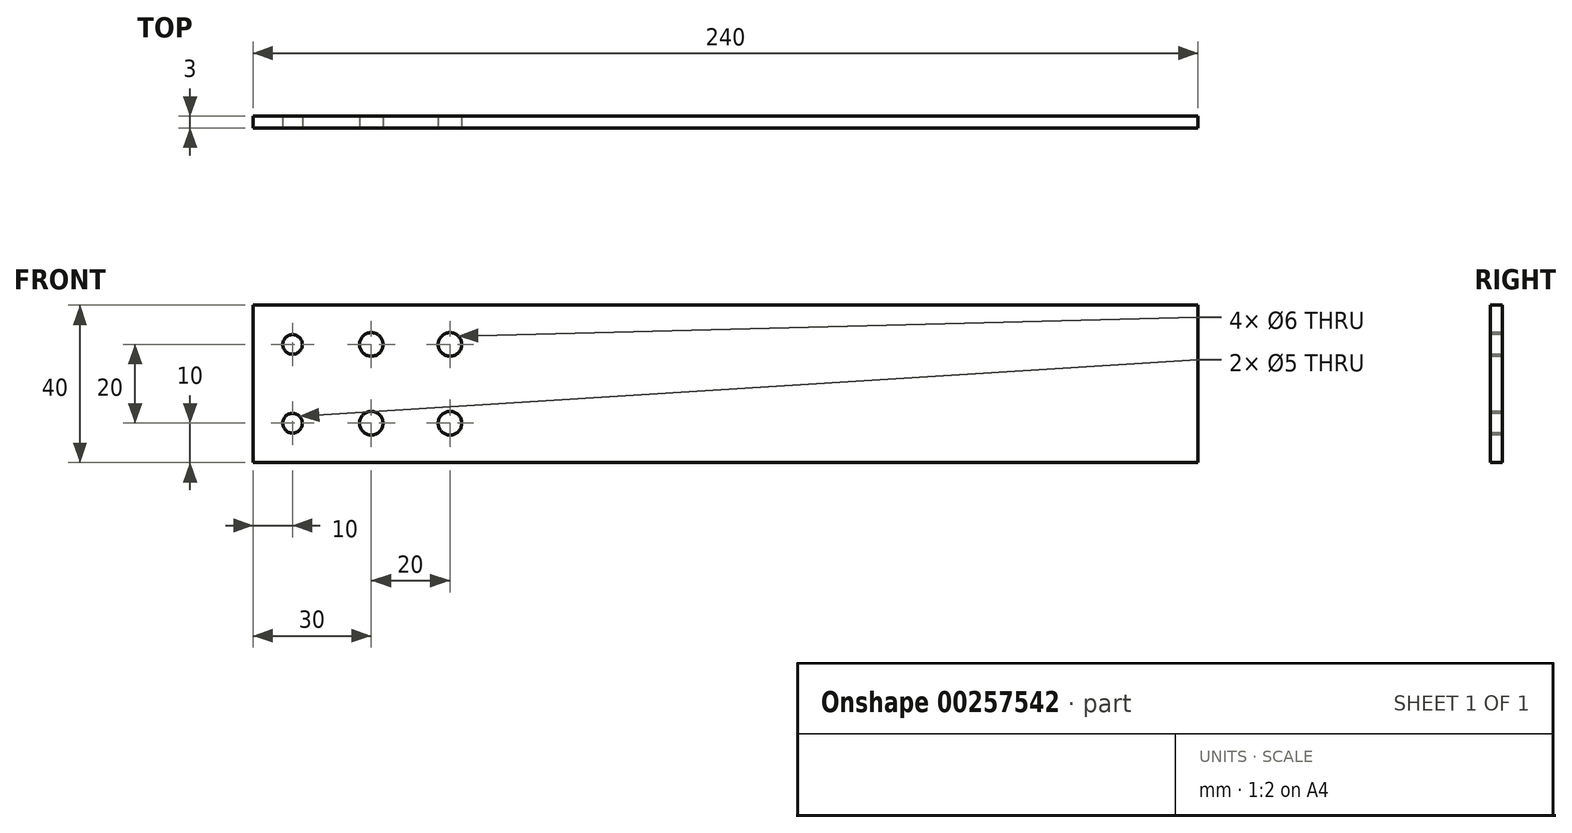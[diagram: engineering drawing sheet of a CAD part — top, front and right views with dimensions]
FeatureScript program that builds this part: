
annotation { "Feature Type Name" : "Feature", "Feature Type Description" : "" }
export const myFeature = defineFeature(function(context is Context, id is Id, definition is map)
    precondition{}
    {
        {
            var Q0;
            Q0=qCreatedBy(makeId("Front.planeOp"),FACE);
            var sketch = newSketch(context, id + "F0", { "sketchPlane" : qUnion([Q0])});
            skLineSegment(sketch, "E0.bottom", {"start": v(120, 20) * mm, "end": v(-120, 20) * mm});
            skLineSegment(sketch, "E0.top", {"start": v(120, -20) * mm, "end": v(-120, -20) * mm});
            skLineSegment(sketch, "E0.left", {"start": v(120, 20) * mm, "end": v(120, -20) * mm});
            skLineSegment(sketch, "E0.right", {"start": v(-120, 20) * mm, "end": v(-120, -20) * mm});
            skPoint(sketch, "E0.middle", {"position": v(0, 0) * mm});
            skSolve(sketch);
        }
        {
            var Q0;
            Q0 = qSketchRegion(id + "F0", true);
            extrude(context, id + "F1", {"entities" : qUnion([Q0]), "depth" : 3 * mm});
        }
        {
            var Q0;
            Q0=makeQuery(id+"F1.opExtrude","CAP_FACE",FACE,{"disambiguationData":[OSD([sQuery(id+"F0.wireOp",EDGE,"E0.bottom"),sQuery(id+"F0.wireOp",EDGE,"E0.top"),sQuery(id+"F0.wireOp",EDGE,"E0.left"),sQuery(id+"F0.wireOp",EDGE,"E0.right")])],"isStart":false});
            var sketch = newSketch(context, id + "F2", { "sketchPlane" : qUnion([Q0])});
            skCircle(sketch, "E1", {"center": v(-110, 10) * mm, "radius": 2.5 * mm});
            skCircle(sketch, "E2", {"center": v(-110, -10) * mm, "radius": 2.5 * mm});
            skSolve(sketch);
        }
        {
            var Q0;
            Q0 = qSketchRegion(id + "F2", true);
            extrude(context, id + "F3", {"entities" : qUnion([Q0]), "operationType" : NewBodyOperationType.REMOVE, "endBound" : BoundingType.THROUGH_ALL, "oppositeDirection" : true, "depth" : 25 * mm});
        }
        {
            var Q0;
            Q0=makeQuery(id+"F1.opExtrude","CAP_FACE",FACE,{"disambiguationData":[OSD([sQuery(id+"F0.wireOp",EDGE,"E0.bottom"),sQuery(id+"F0.wireOp",EDGE,"E0.top"),sQuery(id+"F0.wireOp",EDGE,"E0.left"),sQuery(id+"F0.wireOp",EDGE,"E0.right")])],"isStart":false});
            var sketch = newSketch(context, id + "F4", { "sketchPlane" : qUnion([Q0])});
            skCircle(sketch, "E3.0", {"center": v(-110, 10) * mm, "radius": 2.5 * mm});
            skLineSegment(sketch, "E4.0", {"start": v(-120, 20) * mm, "end": v(-120, -20) * mm});
            skSolve(sketch);
        }
        {
            var Q0;
            Q0=makeQuery(id+"F4.imprint","IMPRINT",FACE,{"disambiguationData":[TD([[makeQuery(id+"F4.imprint","IMPRINT",EDGE,{"derivedFrom":sQuery(id+"F4.wireOp",EDGE,"E3.0")}),-1.0]])]});
            var sketch = newSketch(context, id + "F5", { "sketchPlane" : qUnion([Q0])});
            skCircle(sketch, "E5", {"center": v(-90, 10) * mm, "radius": 3 * mm});
            skCircle(sketch, "E6", {"center": v(-70, 10) * mm, "radius": 3 * mm});
            skCircle(sketch, "E7", {"center": v(-70, -10) * mm, "radius": 3 * mm});
            skCircle(sketch, "E8", {"center": v(-90, -10) * mm, "radius": 3 * mm});
            skCircle(sketch, "E9.0", {"center": v(-110, -10) * mm, "radius": 2.5 * mm});
            skSolve(sketch);
        }
        {
            var Q0;
            Q0 = qSketchRegion(id + "F5", true);
            extrude(context, id + "F6", {"entities" : qUnion([Q0]), "operationType" : NewBodyOperationType.REMOVE, "oppositeDirection" : true, "depth" : 25 * mm});
        }
    });
